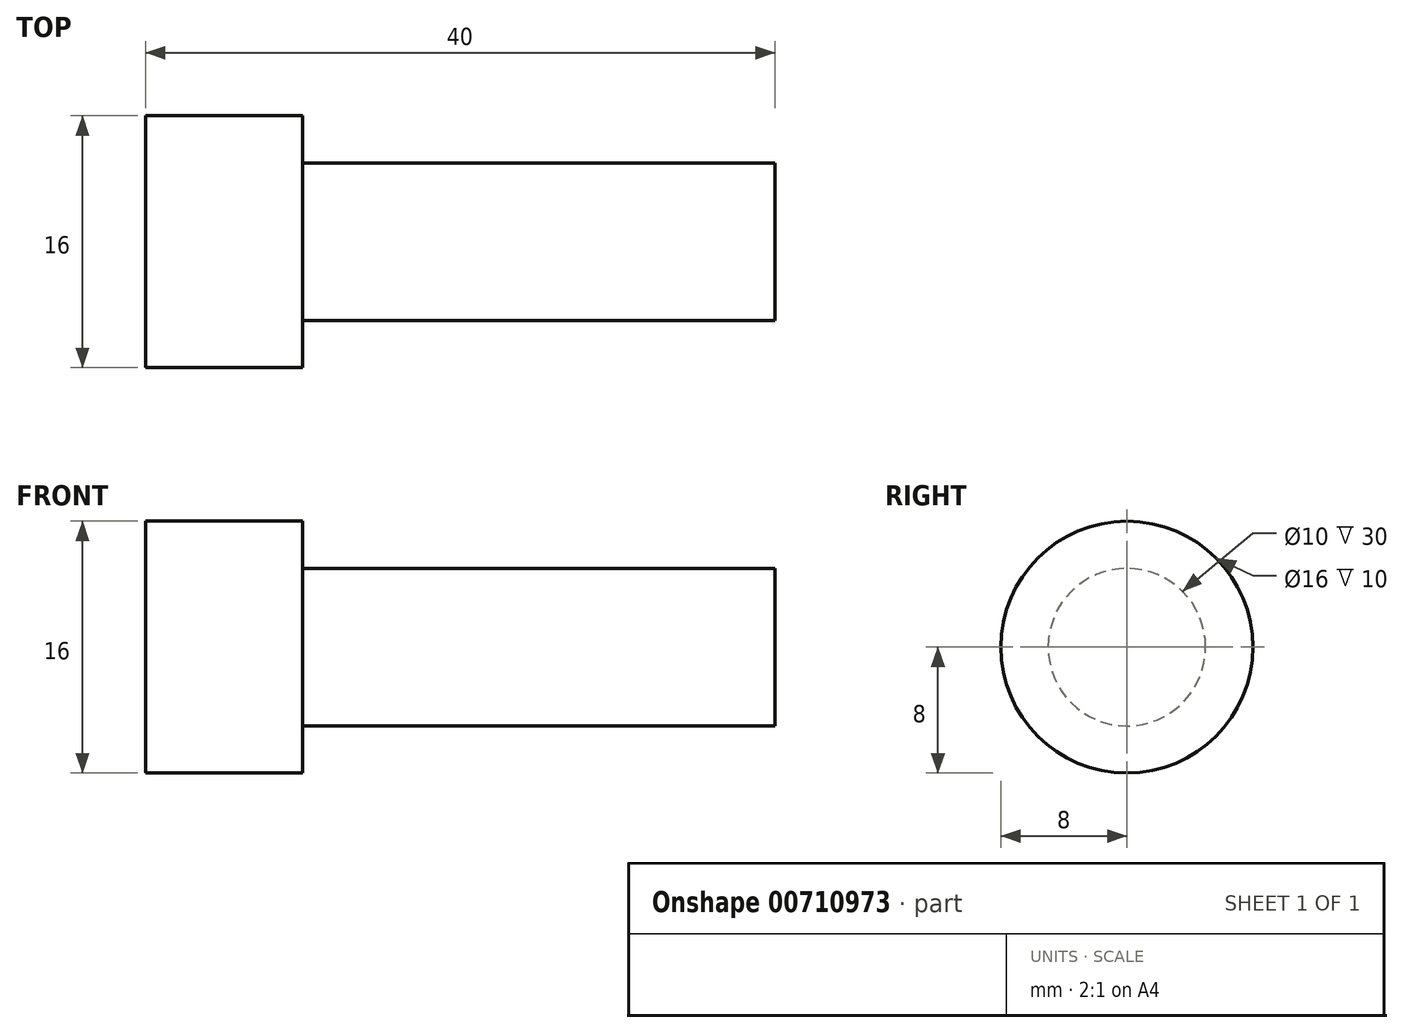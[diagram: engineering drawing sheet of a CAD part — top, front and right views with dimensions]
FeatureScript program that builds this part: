
annotation { "Feature Type Name" : "Feature", "Feature Type Description" : "" }
export const myFeature = defineFeature(function(context is Context, id is Id, definition is map)
    precondition{}
    {
        {
            var Q0;
            Q0=qCreatedBy(makeId("Front.planeOp"),FACE);
            var sketch = newSketch(context, id + "F0", { "sketchPlane" : qUnion([Q0])});
            skLineSegment(sketch, "E0", {"start": v(0, 0) * mm, "end": v(0, 8) * mm});
            skLineSegment(sketch, "E1", {"start": v(0, 8) * mm, "end": v(10, 8) * mm});
            skLineSegment(sketch, "E2", {"start": v(10, 8) * mm, "end": v(10, 5) * mm});
            skLineSegment(sketch, "E3", {"start": v(10, 5) * mm, "end": v(40, 5) * mm});
            skLineSegment(sketch, "E4", {"start": v(40, 5) * mm, "end": v(40, 0) * mm});
            skLineSegment(sketch, "E5", {"start": v(-41.7, 0) * mm, "end": v(43.84, 0) * mm, "construction": true});
            skSolve(sketch);
        }
        {
            var Q0;
            Q0 = qSketchRegion(id + "F0", true);
            var Q1;
            Q1=sQuery(id+"F0.wireOp",EDGE,"E4");
            var Q2;
            Q2=sQuery(id+"F0.wireOp",EDGE,"E3");
            var Q3;
            Q3=sQuery(id+"F0.wireOp",EDGE,"E1");
            var Q4;
            Q4=sQuery(id+"F0.wireOp",EDGE,"E0");
            var Q5;
            Q5=sQuery(id+"F0.wireOp",EDGE,"E2");
            var Q6;
            Q6=sQuery(id+"F0.wireOp",EDGE,"E5");
            revolve(context, id + "F1", {"bodyType" : ToolBodyType.SURFACE, "surfaceOperationType" : NewSurfaceOperationType.NEW, "entities" : qUnion([Q0]), "surfaceEntities" : qUnion([Q1, Q2, Q3, Q4, Q5]), "axis" : qUnion([Q6]), "revolveType" : RevolveType.FULL});
        }
    });
